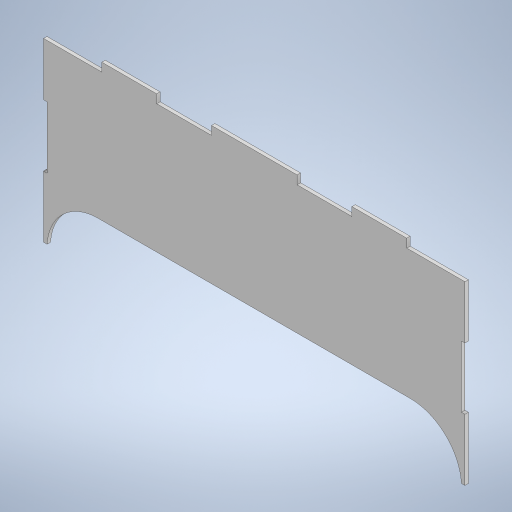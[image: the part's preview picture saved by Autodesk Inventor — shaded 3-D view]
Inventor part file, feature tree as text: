
AUTODESK INVENTOR PART (.ipt)
format: ipt  version: 2023 (Build 270158000, 158)  size: 280,576 bytes
history: native  units: mm
features: extrude x4, sketch x4
ambient origin geometry x8: Origin, YZ Plane, XZ Plane, XY Plane, X Axis, Y Axis, Z Axis, Center Point
bodies: Solid1 (feature_tree)
feature tree (8):
  extrude  "Extrusion1"  Depth=80.0mm
  extrude  "Extrusion2"  Depth=2.0mm TaperAngle=0.0deg
  extrude  "Extrusion3"  Depth=32.0mm
  extrude  "Extrusion4"  Depth=32.0mm
  sketch  "Sketch1"  dims[d0=242.0mm d1=80.0mm]
  sketch  "Sketch2"  dims[d2=30.0mm d3=2.0mm d4=0.0mm]
  sketch  "Sketch3"  dims[d5=32.0mm d6=32.0mm]
  sketch  "Sketch4"  dims[d7=32.0mm d8=32.0mm d9=32.0mm d10=32.0mm d11=50.0mm d12=5.0mm d13=2.0mm d14=0.0mm d26=2.0mm d27=0.0mm d34=31.0mm d35=36.0mm d36=2.0mm d37=2.0mm d39=36.0mm d40=36.0mm d41=2.0mm d42=0.0mm]
